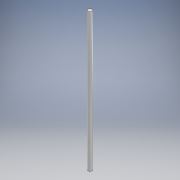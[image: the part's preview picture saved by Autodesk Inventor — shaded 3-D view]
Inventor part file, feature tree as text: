
AUTODESK INVENTOR PART (.ipt)
format: ipt  version: 2017 (Build 210142000, 142)  size: 92,672 bytes
history: native  units: mm
features: extrude x1, sketch x1
ambient origin geometry x8: Origin, YZ Plane, XZ Plane, XY Plane, X Axis, Y Axis, Z Axis, Center Point
bodies: Solid1 (feature_tree)
feature tree (2):
  extrude  "Extrusion1"  Depth=360.0mm TaperAngle=0.0deg
  sketch  "Sketch1"  dims[d0=10.0mm d1=360.0mm d2=0.0mm]
